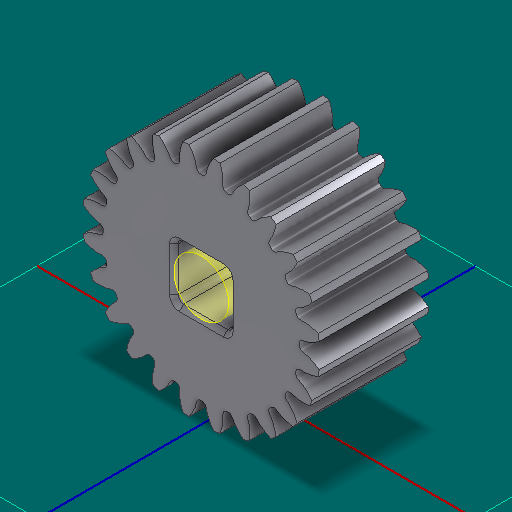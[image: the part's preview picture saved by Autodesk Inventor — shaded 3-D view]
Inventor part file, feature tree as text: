
AUTODESK INVENTOR PART (.ipt)
format: ipt  version: 2025 (Build 290162000, 162)  size: 479,744 bytes
history: native  units: in
note: dims shown in document units (in); Inventor stores cm internally (conversion verified against a paired STEP export)
features: other x5, sketch x1
ambient origin geometry x8: Origin, YZ Plane, XZ Plane, XY Plane, X Axis, Y Axis, Z Axis, Center Point
bodies: Solid1 (feature_tree)
feature tree (6):
  other  "HS 24T Gear, No Insert_mirrored.ipt"
  other  "Solid1::HS 24T Gear, No Insert_mirrored.ipt"
  other  "TaggingFeature1"
  sketch  "Sketch1"  dims[d0=0.3937in]
  other  "Srf1"
  other  "Srf1::Derived"
